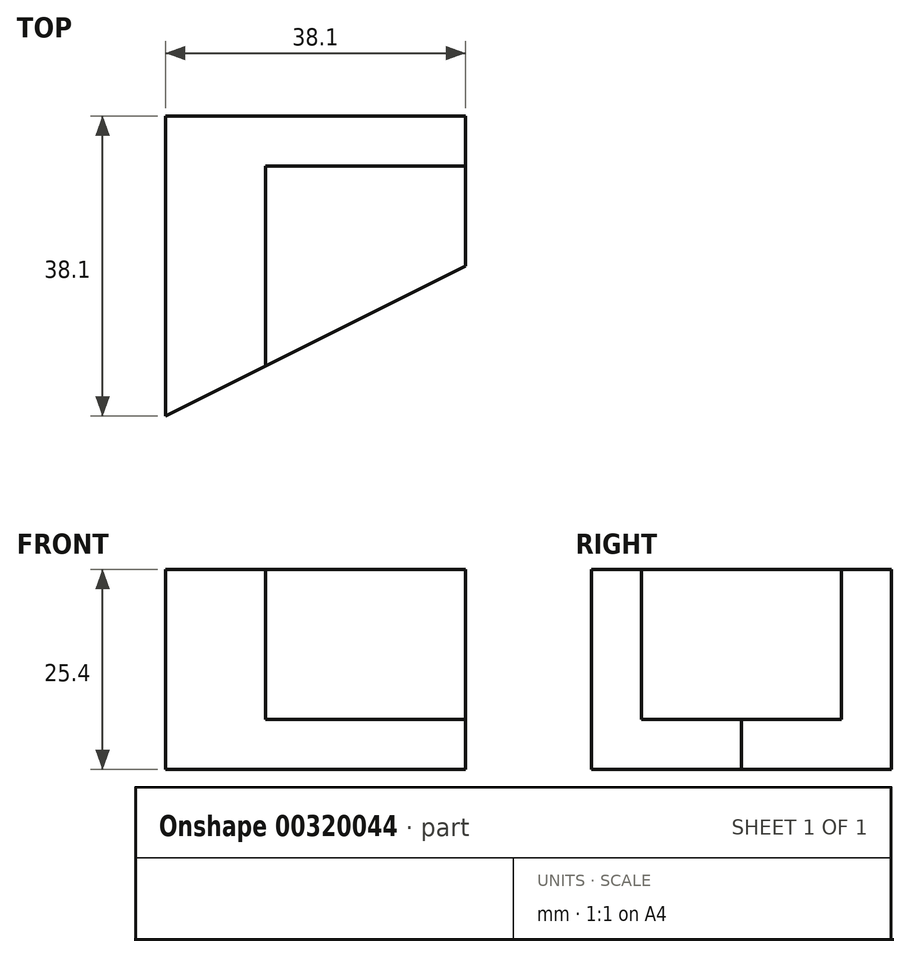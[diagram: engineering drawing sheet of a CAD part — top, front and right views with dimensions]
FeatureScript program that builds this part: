
annotation { "Feature Type Name" : "Feature", "Feature Type Description" : "" }
export const myFeature = defineFeature(function(context is Context, id is Id, definition is map)
    precondition{}
    {
        {
            var Q0;
            Q0=qCreatedBy(makeId("Front.planeOp"),FACE);
            var sketch = newSketch(context, id + "F0", { "sketchPlane" : qUnion([Q0])});
            skLineSegment(sketch, "E0", {"start": v(0, 0) * mm, "end": v(38.1, 0) * mm});
            skLineSegment(sketch, "E1", {"start": v(38.1, 0) * mm, "end": v(38.1, 25.4) * mm});
            skLineSegment(sketch, "E2", {"start": v(38.1, 25.4) * mm, "end": v(0, 25.4) * mm});
            skLineSegment(sketch, "E3", {"start": v(0, 25.4) * mm, "end": v(0, 0) * mm});
            skSolve(sketch);
        }
        {
            var Q0;
            Q0 = qSketchRegion(id + "F0", true);
            extrude(context, id + "F1", {"entities" : qUnion([Q0]), "depth" : 38.1 * mm});
        }
        {
            var Q0;
            Q0=makeQuery(id+"F1.opExtrude","SWEPT_FACE",FACE,{"disambiguationData":[OSD([sQuery(id+"F0.wireOp",EDGE,"E2")])]});
            var sketch = newSketch(context, id + "F2", { "sketchPlane" : qUnion([Q0])});
            skLineSegment(sketch, "E4", {"start": v(38.1, 0) * mm, "end": v(38.1, -19.05) * mm});
            skLineSegment(sketch, "E5", {"start": v(38.1, -19.05) * mm, "end": v(0, -38.1) * mm});
            skLineSegment(sketch, "E6", {"start": v(38.1, -19.05) * mm, "end": v(38.1, -38.1) * mm});
            skLineSegment(sketch, "E7", {"start": v(38.1, -38.1) * mm, "end": v(0, -38.1) * mm});
            skSolve(sketch);
        }
        {
            var Q0;
            Q0 = qSketchRegion(id + "F2", true);
            extrude(context, id + "F3", {"entities" : qUnion([Q0]), "operationType" : NewBodyOperationType.REMOVE, "oppositeDirection" : true, "depth" : 101.6 * mm});
        }
        {
            var Q0;
            Q0=makeQuery(id+"F1.opExtrude","SWEPT_FACE",FACE,{"disambiguationData":[OSD([sQuery(id+"F0.wireOp",EDGE,"E2")])]});
            var sketch = newSketch(context, id + "F4", { "sketchPlane" : qUnion([Q0])});
            skLineSegment(sketch, "E8", {"start": v(38.1, 0) * mm, "end": v(38.1, -6.35) * mm});
            skLineSegment(sketch, "E9", {"start": v(38.1, -6.35) * mm, "end": v(38.1, -19.05) * mm});
            skLineSegment(sketch, "E10", {"start": v(38.1, -19.05) * mm, "end": v(38.1, -6.35) * mm});
            skLineSegment(sketch, "E11", {"start": v(38.1, -6.35) * mm, "end": v(12.7, -6.35) * mm});
            skLineSegment(sketch, "E12", {"start": v(12.7, -6.35) * mm, "end": v(12.7, -31.75) * mm});
            skLineSegment(sketch, "E13", {"start": v(12.7, -31.75) * mm, "end": v(38.1, -19.05) * mm});
            skSolve(sketch);
        }
        {
            var Q0;
            Q0 = qSketchRegion(id + "F4", true);
            extrude(context, id + "F5", {"entities" : qUnion([Q0]), "operationType" : NewBodyOperationType.REMOVE, "oppositeDirection" : true, "depth" : 19.05 * mm});
        }
    });
